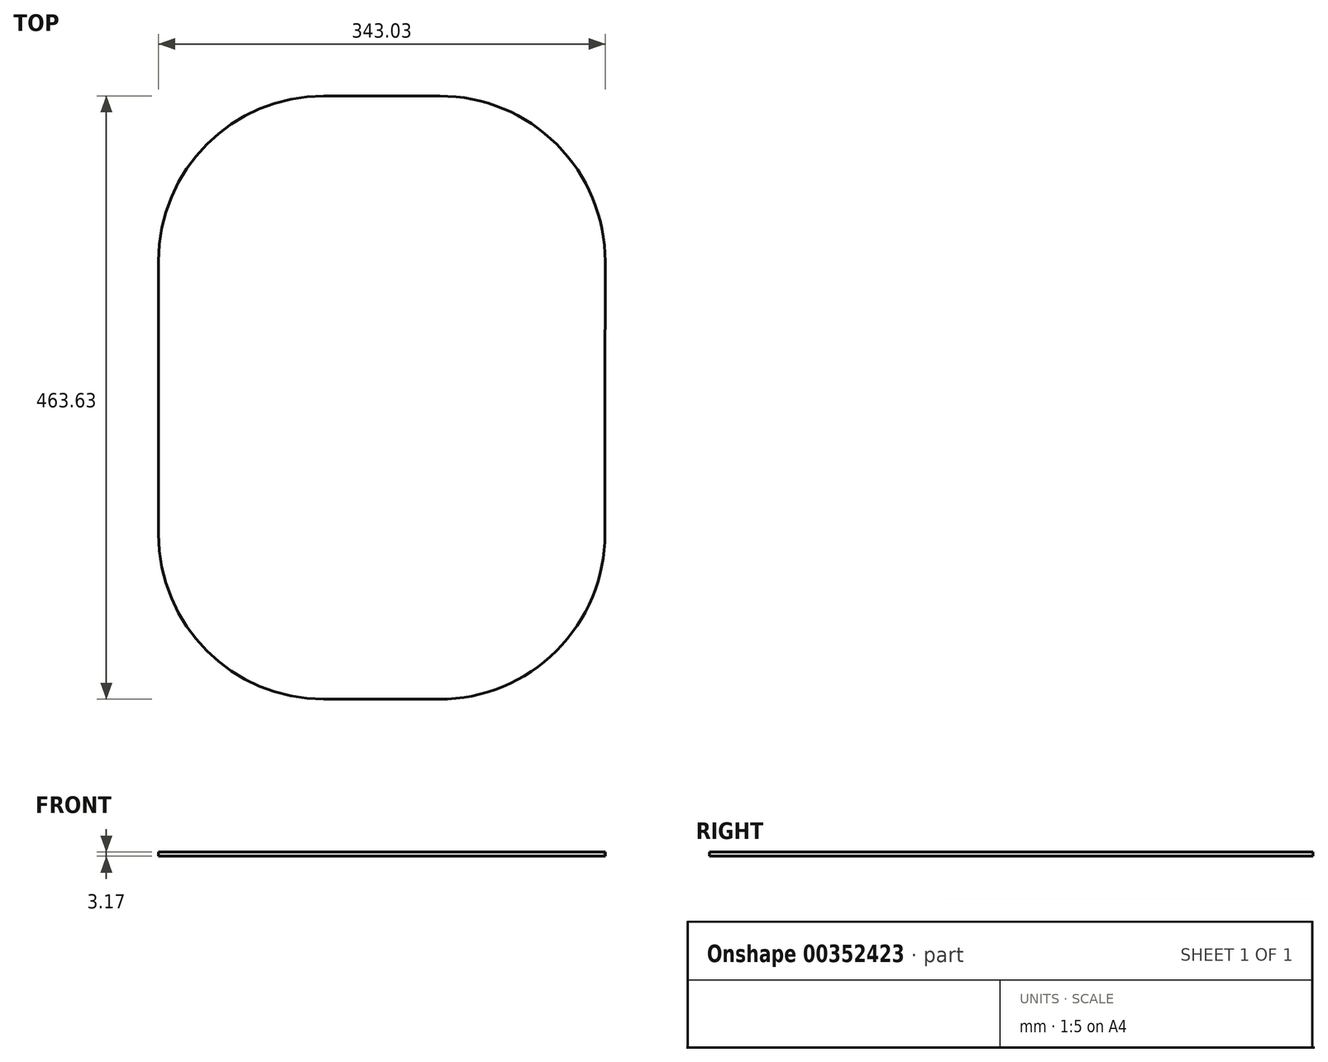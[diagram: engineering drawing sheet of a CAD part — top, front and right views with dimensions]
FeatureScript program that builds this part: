
annotation { "Feature Type Name" : "Feature", "Feature Type Description" : "" }
export const myFeature = defineFeature(function(context is Context, id is Id, definition is map)
    precondition{}
    {
        {
            var Q0;
            Q0=qCreatedBy(makeId("Top.planeOp"),FACE);
            var sketch = newSketch(context, id + "F0", { "sketchPlane" : qUnion([Q0])});
            skLineSegment(sketch, "E0", {"start": v(0, 231.78) * mm, "end": v(0, -231.78) * mm});
            skLineSegment(sketch, "E1", {"start": v(-171.45, 0) * mm, "end": v(171.45, 0) * mm});
            skLineSegment(sketch, "E2", {"start": v(-171.45, 0) * mm, "end": v(-171.45, 104.78) * mm});
            skLineSegment(sketch, "E3", {"start": v(-44.45, 231.78) * mm, "end": v(0, 231.78) * mm});
            skLineSegment(sketch, "E4", {"start": v(171.58, 104.62) * mm, "end": v(171.45, 0) * mm});
            skLineSegment(sketch, "E5", {"start": v(44.24, -231.85) * mm, "end": v(0, -231.78) * mm});
            skLineSegment(sketch, "E6", {"start": v(44.58, 231.78) * mm, "end": v(0, 231.78) * mm});
            skLineSegment(sketch, "E7", {"start": v(171.45, 0) * mm, "end": v(171.45, -104.85) * mm});
            skLineSegment(sketch, "E8", {"start": v(0, -231.78) * mm, "end": v(-44.45, -231.78) * mm});
            skLineSegment(sketch, "E9", {"start": v(-171.45, -104.78) * mm, "end": v(-171.45, 0) * mm});
            skPoint(sketch, "E10.visualSharp", {"position": v(-171.45, 231.78) * mm});
            skArc(sketch, "E10.filletArc", {"start": v(-44.45, 231.78) * mm, "mid": v(-134.25, 194.58) * mm, "end": v(-171.45, 104.78) * mm});
            skPoint(sketch, "E11.visualSharp", {"position": v(171.74, 231.78) * mm});
            skArc(sketch, "E11.filletArc", {"start": v(171.58, 104.62) * mm, "mid": v(134.44, 194.52) * mm, "end": v(44.58, 231.78) * mm});
            skPoint(sketch, "E12.visualSharp", {"position": v(171.45, -232.05) * mm});
            skArc(sketch, "E12.filletArc", {"start": v(44.24, -231.85) * mm, "mid": v(134.18, -194.72) * mm, "end": v(171.45, -104.85) * mm});
            skPoint(sketch, "E13.visualSharp", {"position": v(-171.45, -231.78) * mm});
            skArc(sketch, "E13.filletArc", {"start": v(-171.45, -104.77) * mm, "mid": v(-134.25, -194.58) * mm, "end": v(-44.45, -231.78) * mm});
            skSolve(sketch);
        }
        {
            var Q0;
            {var subQ0=sQuery(id+"F0.wireOp",EDGE,"E2");Q0=makeQuery(id+"F0.imprint","IMPRINT",FACE,{"disambiguationData":[TD([[makeQuery(id+"F0.imprint","IMPRINT",EDGE,{"derivedFrom":subQ0}),-1.0]])]});}
            var Q1;
            {var subQ0=sQuery(id+"F0.wireOp",EDGE,"E4");Q1=makeQuery(id+"F0.imprint","IMPRINT",FACE,{"disambiguationData":[TD([[makeQuery(id+"F0.imprint","IMPRINT",EDGE,{"derivedFrom":subQ0}),-1.0]])]});}
            var Q2;
            {var subQ1=sQuery(id+"F0.wireOp",EDGE,"E5");Q2=makeQuery(id+"F0.imprint","IMPRINT",FACE,{"disambiguationData":[TD([[makeQuery(id+"F0.imprint","IMPRINT",EDGE,{"derivedFrom":subQ1}),-1.0]])]});}
            var Q3;
            {var subQ0=sQuery(id+"F0.wireOp",EDGE,"E8");Q3=makeQuery(id+"F0.imprint","IMPRINT",FACE,{"disambiguationData":[TD([[makeQuery(id+"F0.imprint","IMPRINT",EDGE,{"derivedFrom":subQ0}),-1.0]])]});}
            extrude(context, id + "F1", {"entities" : qUnion([Q0, Q1, Q2, Q3]), "depth" : 3.17 * mm});
        }
    });
